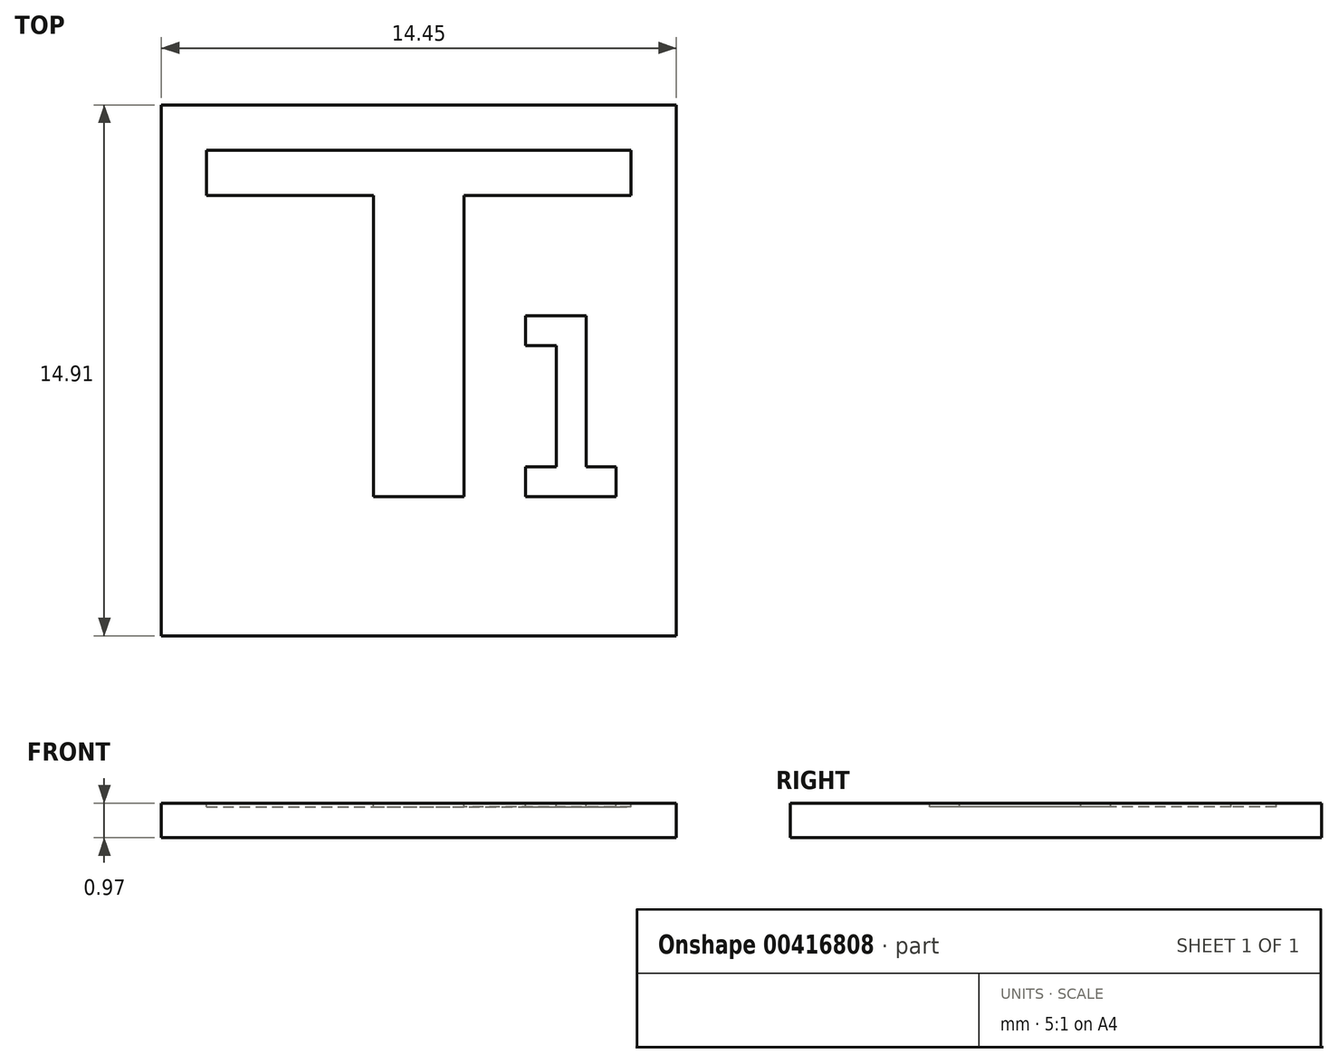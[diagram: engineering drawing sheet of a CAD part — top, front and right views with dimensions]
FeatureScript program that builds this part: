
annotation { "Feature Type Name" : "Feature", "Feature Type Description" : "" }
export const myFeature = defineFeature(function(context is Context, id is Id, definition is map)
    precondition{}
    {
        {
            var Q0;
            Q0=qCreatedBy(makeId("Top.planeOp"),FACE);
            var sketch = newSketch(context, id + "F0", { "sketchPlane" : qUnion([Q0])});
            skLineSegment(sketch, "E0.bottom", {"start": v(0, 0) * mm, "end": v(14.45, 0) * mm});
            skLineSegment(sketch, "E0.top", {"start": v(0, 14.9) * mm, "end": v(14.45, 14.9) * mm});
            skLineSegment(sketch, "E0.left", {"start": v(0, 0) * mm, "end": v(0, 14.9) * mm});
            skLineSegment(sketch, "E0.right", {"start": v(14.45, 0) * mm, "end": v(14.45, 14.9) * mm});
            skSolve(sketch);
        }
        {
            var Q0;
            Q0=makeQuery(id+"F0.imprint","IMPRINT",FACE,{"disambiguationData":[TD([[makeQuery(id+"F0.imprint","IMPRINT",EDGE,{"derivedFrom":sQuery(id+"F0.wireOp",EDGE,"E0.bottom")}),1.0]])]});
            extrude(context, id + "F1", {"entities" : qUnion([Q0]), "depth" : .97 * mm, "offsetDistance" : 25.4 * mm});
        }
        {
            var Q0;
            Q0=makeQuery(id+"F1.opExtrude","CAP_FACE",FACE,{"disambiguationData":[OSD([sQuery(id+"F0.wireOp",EDGE,"E0.bottom"),sQuery(id+"F0.wireOp",EDGE,"E0.top"),sQuery(id+"F0.wireOp",EDGE,"E0.left"),sQuery(id+"F0.wireOp",EDGE,"E0.right")])],"isStart":false});
            var sketch = newSketch(context, id + "F2", { "sketchPlane" : qUnion([Q0])});
            skLineSegment(sketch, "E1", {"start": v(7.22, 14.9) * mm, "end": v(7.22, 0) * mm, "construction": true});
            skLineSegment(sketch, "E2.bottom", {"start": v(1.27, 13.64) * mm, "end": v(13.18, 13.64) * mm});
            skLineSegment(sketch, "E2.left", {"start": v(1.27, 13.64) * mm, "end": v(1.27, 12.37) * mm});
            skLineSegment(sketch, "E2.right", {"start": v(13.18, 13.64) * mm, "end": v(13.18, 12.37) * mm});
            skLineSegment(sketch, "E3", {"start": v(1.27, 12.37) * mm, "end": v(5.95, 12.37) * mm});
            skLineSegment(sketch, "E4", {"start": v(13.18, 12.37) * mm, "end": v(8.5, 12.37) * mm});
            skLineSegment(sketch, "E5", {"start": v(5.95, 12.37) * mm, "end": v(5.95, 3.91) * mm});
            skLineSegment(sketch, "E6", {"start": v(5.95, 3.91) * mm, "end": v(8.5, 3.91) * mm});
            skLineSegment(sketch, "E7", {"start": v(8.5, 3.91) * mm, "end": v(8.5, 12.37) * mm});
            skLineSegment(sketch, "E8.left", {"start": v(11.08, 8.15) * mm, "end": v(11.08, 4.75) * mm});
            skLineSegment(sketch, "E8.right", {"start": v(11.92, 9) * mm, "end": v(11.92, 4.75) * mm});
            skLineSegment(sketch, "E9.top", {"start": v(11.08, 8.15) * mm, "end": v(10.22, 8.15) * mm});
            skLineSegment(sketch, "E9.right", {"start": v(10.22, 9) * mm, "end": v(10.22, 8.15) * mm});
            skLineSegment(sketch, "E10.bottom", {"start": v(10.22, 4.75) * mm, "end": v(11.08, 4.75) * mm});
            skLineSegment(sketch, "E10.top", {"start": v(10.22, 3.91) * mm, "end": v(12.76, 3.91) * mm});
            skLineSegment(sketch, "E10.left", {"start": v(10.22, 4.75) * mm, "end": v(10.22, 3.91) * mm});
            skLineSegment(sketch, "E10.right", {"start": v(12.76, 4.75) * mm, "end": v(12.76, 3.91) * mm});
            skLineSegment(sketch, "E11.trimOffspring", {"start": v(11.92, 4.75) * mm, "end": v(12.76, 4.75) * mm});
            skLineSegment(sketch, "E12", {"start": v(10.22, 9) * mm, "end": v(11.92, 9) * mm});
            skSolve(sketch);
        }
        {
            var Q0;
            Q0 = qSketchRegion(id + "F2", true);
            extrude(context, id + "F3", {"entities" : qUnion([Q0]), "operationType" : NewBodyOperationType.REMOVE, "oppositeDirection" : true, "depth" : .1 * mm, "offsetDistance" : 25.4 * mm});
        }
    });
